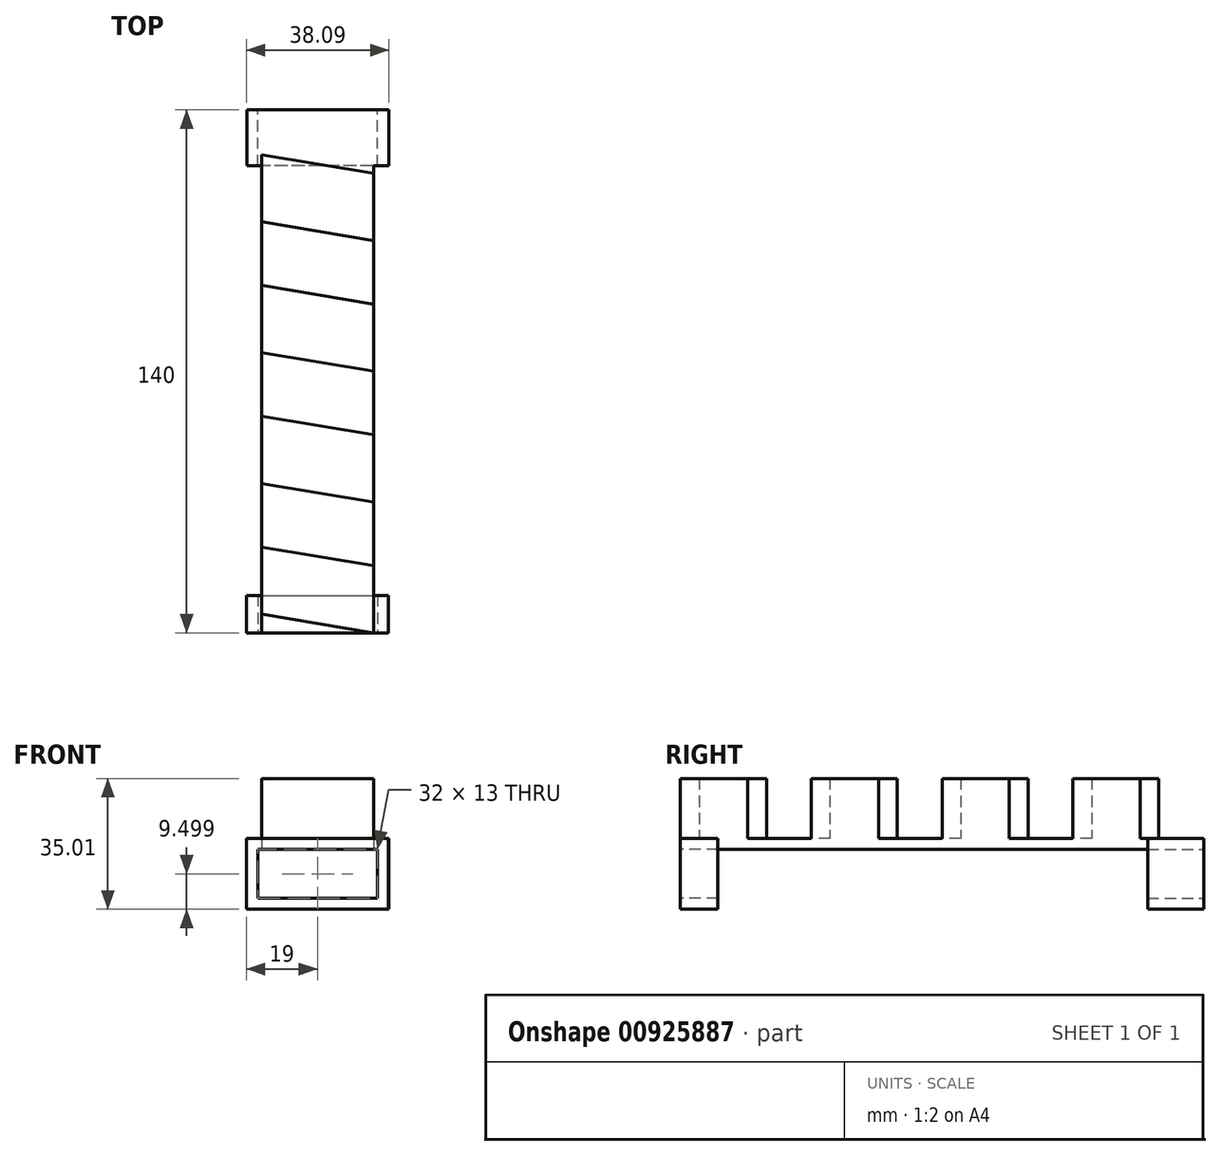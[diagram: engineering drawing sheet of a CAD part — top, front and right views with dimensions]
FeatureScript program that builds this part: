
annotation { "Feature Type Name" : "Feature", "Feature Type Description" : "" }
export const myFeature = defineFeature(function(context is Context, id is Id, definition is map)
    precondition{}
    {
        {
            var Q0;
            Q0=qCreatedBy(makeId("Top.planeOp"),FACE);
            var sketch = newSketch(context, id + "F0", { "sketchPlane" : qUnion([Q0])});
            skLineSegment(sketch, "E0.bottom", {"start": v(12.89, 94.25) * mm, "end": v(42.89, 94.25) * mm});
            skLineSegment(sketch, "E0.top", {"start": v(12.89, -45.75) * mm, "end": v(42.89, -45.75) * mm});
            skLineSegment(sketch, "E0.left", {"start": v(12.89, 94.25) * mm, "end": v(12.89, -45.75) * mm});
            skLineSegment(sketch, "E0.right", {"start": v(42.89, 94.25) * mm, "end": v(42.89, -45.75) * mm});
            skSolve(sketch);
        }
        {
            var Q0;
            Q0=makeQuery(id+"F0.imprint","IMPRINT",FACE,{"disambiguationData":[TD([[makeQuery(id+"F0.imprint","IMPRINT",EDGE,{"derivedFrom":sQuery(id+"F0.wireOp",EDGE,"E0.bottom")}),-1.0]])]});
            extrude(context, id + "F1", {"entities" : qUnion([Q0]), "depth" : 3 * mm, "offsetDistance" : 25 * mm});
        }
        {
            var Q0;
            Q0=makeQuery(id+"F1.opExtrude","CAP_FACE",FACE,{"disambiguationData":[OSD([sQuery(id+"F0.wireOp",EDGE,"E0.bottom"),sQuery(id+"F0.wireOp",EDGE,"E0.top"),sQuery(id+"F0.wireOp",EDGE,"E0.left"),sQuery(id+"F0.wireOp",EDGE,"E0.right")])],"isStart":false});
            var sketch = newSketch(context, id + "F2", { "sketchPlane" : qUnion([Q0])});
            skLineSegment(sketch, "E1", {"start": v(12.89, -22.75) * mm, "end": v(42.89, -27.75) * mm});
            skLineSegment(sketch, "E2.0.1.0", {"start": v(12.89, -5.75) * mm, "end": v(42.89, -10.75) * mm});
            skLineSegment(sketch, "E2.0.2.0", {"start": v(12.89, 12.25) * mm, "end": v(42.89, 7.25) * mm});
            skLineSegment(sketch, "E2.0.3.0", {"start": v(12.89, 29.25) * mm, "end": v(42.89, 24.25) * mm});
            skLineSegment(sketch, "E2.0.4.0", {"start": v(12.89, 47.25) * mm, "end": v(42.89, 42.25) * mm});
            skLineSegment(sketch, "E2.direction1", {"start": v(12.89, -22.75) * mm, "end": v(37.89, -22.75) * mm, "construction": true});
            skLineSegment(sketch, "E2.direction2", {"start": v(12.89, -22.75) * mm, "end": v(12.89, -5.75) * mm, "construction": true});
            skLineSegment(sketch, "E3.0.4.0", {"start": v(12.89, 64.25) * mm, "end": v(42.89, 59.25) * mm});
            skLineSegment(sketch, "E4.0.4.0", {"start": v(12.89, 82.25) * mm, "end": v(42.89, 77.25) * mm});
            skLineSegment(sketch, "E5", {"start": v(12.89, -40.75) * mm, "end": v(42.89, -45.75) * mm});
            skSolve(sketch);
        }
        {
            var Q0;
            {var subQ0=sQuery(id+"F2.wireOp",EDGE,"E1");Q0=makeQuery(id+"F2.imprint","IMPRINT",FACE,{"disambiguationData":[TD([[makeQuery(id+"F2.imprint","IMPRINT",EDGE,{"derivedFrom":subQ0}),-1.0]])]});}
            var Q1;
            {var subQ0=sQuery(id+"F2.wireOp",EDGE,"E2.0.1.0");Q1=makeQuery(id+"F2.imprint","IMPRINT",FACE,{"disambiguationData":[TD([[makeQuery(id+"F2.imprint","IMPRINT",EDGE,{"derivedFrom":subQ0}),1.0]])]});}
            var Q2;
            {var subQ0=sQuery(id+"F2.wireOp",EDGE,"E2.0.3.0");Q2=makeQuery(id+"F2.imprint","IMPRINT",FACE,{"disambiguationData":[TD([[makeQuery(id+"F2.imprint","IMPRINT",EDGE,{"derivedFrom":subQ0}),1.0]])]});}
            var Q3;
            {var subQ0=sQuery(id+"F2.wireOp",EDGE,"E3.0.4.0");Q3=makeQuery(id+"F2.imprint","IMPRINT",FACE,{"disambiguationData":[TD([[makeQuery(id+"F2.imprint","IMPRINT",EDGE,{"derivedFrom":subQ0}),1.0]])]});}
            extrude(context, id + "F3", {"entities" : qUnion([Q0, Q1, Q2, Q3]), "operationType" : NewBodyOperationType.ADD, "depth" : 16 * mm, "offsetDistance" : 25 * mm});
        }
        {
            var Q0;
            Q0=makeQuery(id+"F1.opExtrude","SWEPT_FACE",FACE,{"disambiguationData":[OSD([sQuery(id+"F0.wireOp",EDGE,"E0.bottom")])]});
            var sketch = newSketch(context, id + "F4", { "sketchPlane" : qUnion([Q0])});
            skLineSegment(sketch, "E6.bottom", {"start": v(-46.89, 3) * mm, "end": v(-43.89, 3) * mm});
            skLineSegment(sketch, "E6.top", {"start": v(-46.89, -16) * mm, "end": v(-43.89, -16) * mm});
            skLineSegment(sketch, "E6.left", {"start": v(-46.89, 3) * mm, "end": v(-46.89, -16) * mm});
            skLineSegment(sketch, "E6.right", {"start": v(-43.89, 3) * mm, "end": v(-43.89, -16) * mm});
            skLineSegment(sketch, "E7.bottom", {"start": v(-43.89, -16) * mm, "end": v(-11.89, -16) * mm});
            skLineSegment(sketch, "E7.top", {"start": v(-43.89, -13) * mm, "end": v(-11.89, -13) * mm});
            skLineSegment(sketch, "E7.left", {"start": v(-43.89, -13) * mm, "end": v(-43.89, -16) * mm});
            skLineSegment(sketch, "E7.right", {"start": v(-11.89, -13) * mm, "end": v(-11.89, -16) * mm});
            skLineSegment(sketch, "E8.bottom", {"start": v(-11.89, 3) * mm, "end": v(-8.89, 3) * mm});
            skLineSegment(sketch, "E8.top", {"start": v(-11.89, -16) * mm, "end": v(-8.89, -16) * mm});
            skLineSegment(sketch, "E8.left", {"start": v(-11.89, 3) * mm, "end": v(-11.89, -16) * mm});
            skLineSegment(sketch, "E8.right", {"start": v(-8.89, 3) * mm, "end": v(-8.89, -16) * mm});
            skLineSegment(sketch, "E9.bottom", {"start": v(-46.89, 3) * mm, "end": v(-8.89, 3) * mm});
            skLineSegment(sketch, "E9.top", {"start": v(-46.89, 0) * mm, "end": v(-8.89, 0) * mm});
            skLineSegment(sketch, "E9.left", {"start": v(-46.89, 3) * mm, "end": v(-46.89, 0) * mm});
            skLineSegment(sketch, "E9.right", {"start": v(-8.89, 3) * mm, "end": v(-8.89, 0) * mm});
            skSolve(sketch);
        }
        {
            var Q0;
            {var subQ0=sQuery(id+"F4.wireOp",EDGE,"E7.bottom");Q0=makeQuery(id+"F4.imprint","IMPRINT",FACE,{"disambiguationData":[TD([[makeQuery(id+"F4.imprint","IMPRINT",EDGE,{"derivedFrom":subQ0}),1.0]])]});}
            var Q1;
            {var subQ4=sQuery(id+"F4.wireOp",EDGE,"E6.bottom");Q1=makeQuery(id+"F4.imprint","IMPRINT",FACE,{"disambiguationData":[TD([[makeQuery(id+"F4.imprint","IMPRINT",EDGE,{"derivedFrom":subQ4}),-1.0]])]});}
            var Q2;
            {var subQ1=sQuery(id+"F4.wireOp",EDGE,"E7.right");Q2=makeQuery(id+"F4.imprint","IMPRINT",FACE,{"disambiguationData":[TD([[makeQuery(id+"F4.imprint","IMPRINT",EDGE,{"derivedFrom":subQ1}),1.0]])]});}
            var Q3;
            {var subQ5=sQuery(id+"F4.wireOp",EDGE,"E6.top");Q3=makeQuery(id+"F4.imprint","IMPRINT",FACE,{"disambiguationData":[TD([[makeQuery(id+"F4.imprint","IMPRINT",EDGE,{"derivedFrom":subQ5}),1.0]])]});}
            var Q4;
            {var subQ5=makeQuery(id+"F1.opExtrude","SWEPT_EDGE",EDGE,{"disambiguationData":[OSD([sQuery(id+"F0.wireOp",EDGE,"E0.bottom"),sQuery(id+"F0.wireOp",EDGE,"E0.right")])]});Q4=makeQuery(id+"F4.imprint","IMPRINT",FACE,{"disambiguationData":[TD([[makeQuery(id+"F4.imprint","IMPRINT",EDGE,{"derivedFrom":subQ5}),-1.0]])]});}
            var Q5;
            {var subQ0=sQuery(id+"F4.wireOp",EDGE,"E8.bottom");Q5=makeQuery(id+"F4.imprint","IMPRINT",FACE,{"disambiguationData":[TD([[makeQuery(id+"F4.imprint","IMPRINT",EDGE,{"derivedFrom":subQ0}),-1.0]])]});}
            var Q6;
            {var subQ5=makeQuery(id+"F1.opExtrude","SWEPT_EDGE",EDGE,{"disambiguationData":[OSD([sQuery(id+"F0.wireOp",EDGE,"E0.bottom"),sQuery(id+"F0.wireOp",EDGE,"E0.left")])]});Q6=makeQuery(id+"F4.imprint","IMPRINT",FACE,{"disambiguationData":[TD([[makeQuery(id+"F4.imprint","IMPRINT",EDGE,{"derivedFrom":subQ5}),1.0]])]});}
            var Q7;
            {var subQ1=sQuery(id+"F4.wireOp",EDGE,"E7.right");Q7=makeQuery(id+"F4.imprint","IMPRINT",FACE,{"disambiguationData":[TD([[makeQuery(id+"F4.imprint","IMPRINT",EDGE,{"derivedFrom":subQ1}),1.0]])]});}
            var Q8;
            {var subQ0=sQuery(id+"F4.wireOp",EDGE,"E6.bottom");Q8=makeQuery(id+"F4.imprint","IMPRINT",FACE,{"disambiguationData":[TD([[makeQuery(id+"F4.imprint","IMPRINT",EDGE,{"derivedFrom":subQ0}),-1.0]])]});}
            extrude(context, id + "F5", {"entities" : qUnion([Q0, Q1, Q2, Q3, Q4, Q5, Q6, Q7, Q8]), "operationType" : NewBodyOperationType.ADD, "oppositeDirection" : true, "depth" : 15 * mm, "offsetDistance" : 25 * mm});
        }
        {
            var Q0;
            Q0=makeQuery(id+"F1.opExtrude","SWEPT_FACE",FACE,{"disambiguationData":[OSD([sQuery(id+"F0.wireOp",EDGE,"E0.top")])]});
            var sketch = newSketch(context, id + "F6", { "sketchPlane" : qUnion([Q0])});
            skLineSegment(sketch, "E10.bottom", {"start": v(8.8, 2.99) * mm, "end": v(11.8, 2.99) * mm});
            skLineSegment(sketch, "E10.top", {"start": v(8.8, -16.01) * mm, "end": v(11.8, -16.01) * mm});
            skLineSegment(sketch, "E10.left", {"start": v(8.8, 2.99) * mm, "end": v(8.8, -16.01) * mm});
            skLineSegment(sketch, "E10.right", {"start": v(11.8, 2.99) * mm, "end": v(11.8, -16.01) * mm});
            skLineSegment(sketch, "E11.bottom", {"start": v(11.8, -16.01) * mm, "end": v(43.8, -16.01) * mm});
            skLineSegment(sketch, "E11.top", {"start": v(11.8, -13.01) * mm, "end": v(43.8, -13.01) * mm});
            skLineSegment(sketch, "E11.left", {"start": v(11.8, -13.01) * mm, "end": v(11.8, -16.01) * mm});
            skLineSegment(sketch, "E11.right", {"start": v(43.8, -13.01) * mm, "end": v(43.8, -16.01) * mm});
            skLineSegment(sketch, "E12.bottom", {"start": v(43.8, 2.99) * mm, "end": v(46.8, 2.99) * mm});
            skLineSegment(sketch, "E12.top", {"start": v(43.8, -16.01) * mm, "end": v(46.8, -16.01) * mm});
            skLineSegment(sketch, "E12.left", {"start": v(43.8, 2.99) * mm, "end": v(43.8, -16.01) * mm});
            skLineSegment(sketch, "E12.right", {"start": v(46.8, 2.99) * mm, "end": v(46.8, -16.01) * mm});
            skLineSegment(sketch, "E13.bottom", {"start": v(8.8, 2.99) * mm, "end": v(46.8, 2.99) * mm});
            skLineSegment(sketch, "E13.top", {"start": v(8.8, -0.01) * mm, "end": v(46.8, -0.01) * mm});
            skLineSegment(sketch, "E13.left", {"start": v(8.8, 2.99) * mm, "end": v(8.8, -0.01) * mm});
            skLineSegment(sketch, "E13.right", {"start": v(46.8, 2.99) * mm, "end": v(46.8, -0.01) * mm});
            skSolve(sketch);
        }
        {
            var Q0;
            {var subQ0=sQuery(id+"F6.wireOp",EDGE,"E10.bottom");Q0=makeQuery(id+"F6.imprint","IMPRINT",FACE,{"disambiguationData":[TD([[makeQuery(id+"F6.imprint","IMPRINT",EDGE,{"derivedFrom":subQ0}),-1.0]])]});}
            var Q1;
            {var subQ5=sQuery(id+"F6.wireOp",EDGE,"E10.top");Q1=makeQuery(id+"F6.imprint","IMPRINT",FACE,{"disambiguationData":[TD([[makeQuery(id+"F6.imprint","IMPRINT",EDGE,{"derivedFrom":subQ5}),1.0]])]});}
            var Q2;
            {var subQ0=sQuery(id+"F6.wireOp",EDGE,"E11.bottom");Q2=makeQuery(id+"F6.imprint","IMPRINT",FACE,{"disambiguationData":[TD([[makeQuery(id+"F6.imprint","IMPRINT",EDGE,{"derivedFrom":subQ0}),1.0]])]});}
            var Q3;
            {var subQ1=sQuery(id+"F6.wireOp",EDGE,"E11.right");Q3=makeQuery(id+"F6.imprint","IMPRINT",FACE,{"disambiguationData":[TD([[makeQuery(id+"F6.imprint","IMPRINT",EDGE,{"derivedFrom":subQ1}),1.0]])]});}
            var Q4;
            {var subQ0=sQuery(id+"F6.wireOp",EDGE,"E12.bottom");Q4=makeQuery(id+"F6.imprint","IMPRINT",FACE,{"disambiguationData":[TD([[makeQuery(id+"F6.imprint","IMPRINT",EDGE,{"derivedFrom":subQ0}),-1.0]])]});}
            var Q5;
            {var subQ3=sQuery(id+"F0.wireOp",EDGE,"E0.top");var subQ8=makeQuery(id+"F1.opExtrude","CAP_EDGE",EDGE,{"disambiguationData":[OSD([subQ3])],"isStart":true});Q5=makeQuery(id+"F6.imprint","IMPRINT",FACE,{"disambiguationData":[TD([[makeQuery(id+"F6.imprint","IMPRINT",EDGE,{"derivedFrom":subQ8}),-1.0]])]});}
            extrude(context, id + "F7", {"entities" : qUnion([Q0, Q1, Q2, Q3, Q4, Q5]), "operationType" : NewBodyOperationType.ADD, "oppositeDirection" : true, "depth" : 10 * mm, "offsetDistance" : 25 * mm});
        }
    });
